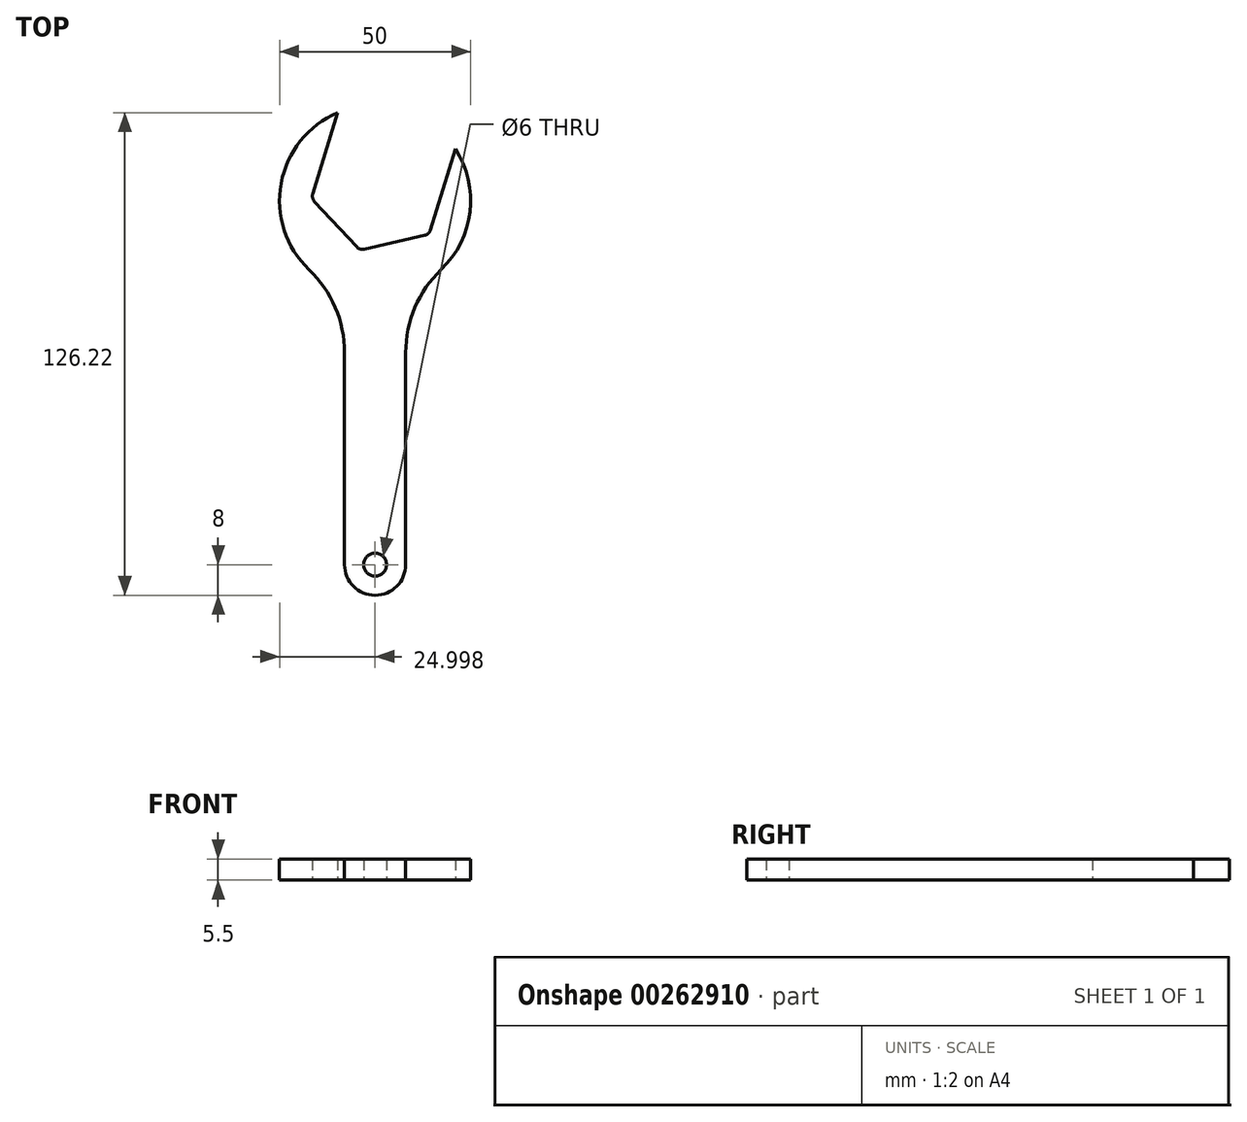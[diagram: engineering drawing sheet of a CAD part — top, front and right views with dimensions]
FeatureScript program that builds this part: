
annotation { "Feature Type Name" : "Feature", "Feature Type Description" : "" }
export const myFeature = defineFeature(function(context is Context, id is Id, definition is map)
    precondition{}
    {
        {
            var Q0;
            Q0=qCreatedBy(makeId("Top.planeOp"),FACE);
            var sketch = newSketch(context, id + "F0", { "sketchPlane" : qUnion([Q0])});
            skCircle(sketch, "E0.cCircle", {"center": v(0, 0) * mm, "radius": 16.1 * mm, "construction": true});
            skLineSegment(sketch, "E0.0", {"start": v(19.53, 8.8) * mm, "end": v(13.02, -12.5) * mm});
            skLineSegment(sketch, "E0.1", {"start": v(11.55, -13.86) * mm, "end": v(-4.31, -17.52) * mm});
            skLineSegment(sketch, "E0.2", {"start": v(-6.22, -16.93) * mm, "end": v(-17.33, -5.03) * mm});
            skLineSegment(sketch, "E0.3", {"start": v(-17.78, -3.08) * mm, "end": v(-11.27, 18.22) * mm});
            skLineSegment(sketch, "E0.4", {"start": v(-12.68, 13.6) * mm, "end": v(5.44, 17.78) * mm, "construction": true});
            skLineSegment(sketch, "E0.5", {"start": v(5.44, 17.78) * mm, "end": v(18.11, 4.18) * mm, "construction": true});
            skPoint(sketch, "E0.0.midPoint", {"position": v(15.4, -4.7) * mm});
            skArc(sketch, "E1", {"start": v(-9.46, -100) * mm, "mid": v(-1.46, -108) * mm, "end": v(6.54, -100) * mm});
            skLineSegment(sketch, "E2.trimOffspring", {"start": v(6.54, -44.54) * mm, "end": v(6.54, -100) * mm});
            skLineSegment(sketch, "E3.trimOffspring", {"start": v(-9.46, -44.54) * mm, "end": v(-9.46, -100) * mm});
            skCircle(sketch, "E4", {"center": v(-1.46, -100) * mm, "radius": 3 * mm});
            skPoint(sketch, "E5.visualSharp", {"position": v(18.11, 4.18) * mm});
            skPoint(sketch, "E6.visualSharp", {"position": v(-12.68, 13.6) * mm});
            skLineSegment(sketch, "E7", {"start": v(-4.7, -15.4) * mm, "end": v(4.7, 15.4) * mm, "construction": true});
            skArc(sketch, "E8", {"start": v(15.81, -22.86) * mm, "mid": v(23.37, -7.7) * mm, "end": v(19.53, 8.8) * mm});
            skArc(sketch, "E9", {"start": v(-9.46, -28.47) * mm, "mid": v(-1.46, -29.78) * mm, "end": v(6.54, -28.47) * mm, "construction": true});
            skLineSegment(sketch, "E10", {"start": v(-1.46, -4.78) * mm, "end": v(-1.46, -100) * mm, "construction": true});
            skLineSegment(sketch, "E11", {"start": v(-11.27, 18.22) * mm, "end": v(-11.27, 18.22) * mm});
            skArc(sketch, "E12", {"start": v(-11.27, 18.22) * mm, "mid": v(-26.06, -0.3) * mm, "end": v(-18.73, -22.86) * mm});
            skArc(sketch, "E13", {"start": v(19.53, 8.8) * mm, "mid": v(5.85, 19.13) * mm, "end": v(-11.27, 18.22) * mm, "construction": true});
            skPoint(sketch, "E14.visualSharp", {"position": v(6.54, -28.47) * mm});
            skArc(sketch, "E14.filletArc", {"start": v(15.81, -22.86) * mm, "mid": v(8.95, -32.75) * mm, "end": v(6.54, -44.54) * mm});
            skPoint(sketch, "E15.visualSharp", {"position": v(-9.46, -28.47) * mm});
            skArc(sketch, "E15.filletArc", {"start": v(-9.46, -44.54) * mm, "mid": v(-11.88, -32.75) * mm, "end": v(-18.73, -22.86) * mm});
            skPoint(sketch, "E16.visualSharp", {"position": v(-18.11, -4.18) * mm});
            skArc(sketch, "E16.filletArc", {"start": v(-17.78, -3.08) * mm, "mid": v(-17.81, -4.11) * mm, "end": v(-17.33, -5.03) * mm});
            skPoint(sketch, "E17.visualSharp", {"position": v(-5.44, -17.78) * mm});
            skArc(sketch, "E17.filletArc", {"start": v(-6.22, -16.93) * mm, "mid": v(-5.34, -17.48) * mm, "end": v(-4.31, -17.52) * mm});
            skPoint(sketch, "E18.visualSharp", {"position": v(12.68, -13.6) * mm});
            skArc(sketch, "E18.filletArc", {"start": v(11.55, -13.86) * mm, "mid": v(12.47, -13.37) * mm, "end": v(13.02, -12.5) * mm});
            skSolve(sketch);
        }
        {
            var Q0;
            Q0=qSketchRegion(id+"F0",true);
            extrude(context, id + "F1", {"entities" : qUnion([Q0]), "depth" : 5.5 * mm});
        }
    });
